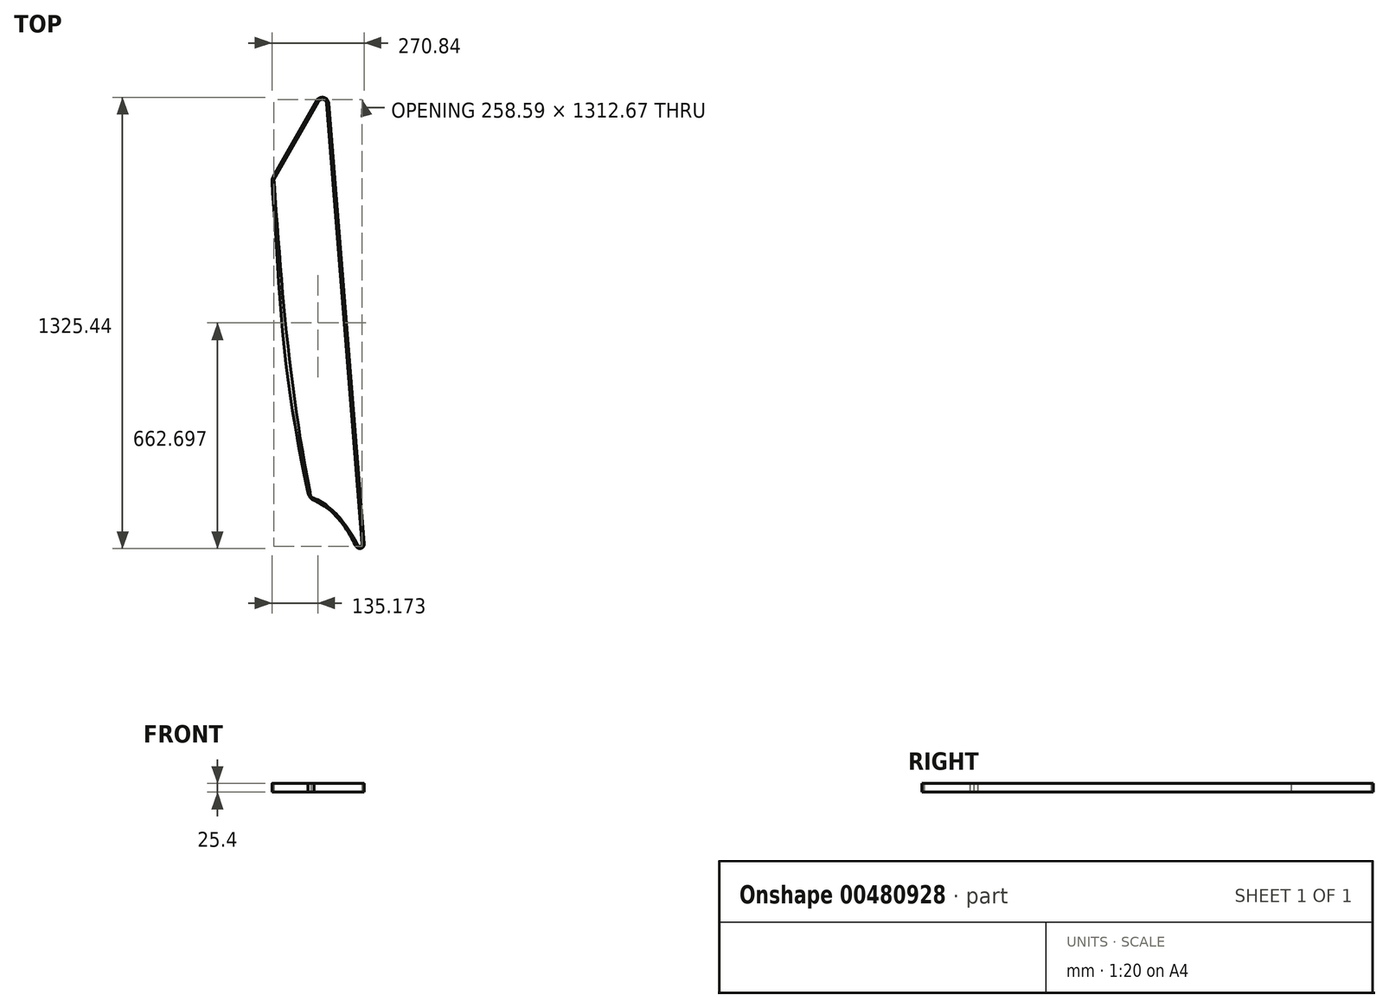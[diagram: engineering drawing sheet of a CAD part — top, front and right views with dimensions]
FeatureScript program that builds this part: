
annotation { "Feature Type Name" : "Feature", "Feature Type Description" : "" }
export const myFeature = defineFeature(function(context is Context, id is Id, definition is map)
    precondition{}
    {
        {
            var Q0;
            Q0=qCreatedBy(makeId("Top.planeOp"),FACE);
            var sketch = newSketch(context, id + "F0", { "sketchPlane" : qUnion([Q0])});
            skLineSegment(sketch, "E0", {"start": v(-2.57, 32.08) * mm, "end": v(-106.43, 1326.28) * mm});
            skFitSpline(sketch, "E1", {"points": [v(-109.71, 1367.2) * mm, v(-261.16, 1102.61) * mm], "startDerivative": vector(-151.45, -264.6) * mm, "endDerivative": vector(-151.45, -264.6) * mm});
            skFitSpline(sketch, "E2", {"points": [v(0, 0) * mm, v(-152.49, 170.33) * mm], "startDerivative": vector(-122.88, 253.62) * mm, "endDerivative": vector(-197.32, 68.63) * mm});
            skFitSpline(sketch, "E3", {"points": [v(-152.49, 170.33) * mm, v(-261.16, 1102.61) * mm], "startDerivative": vector(-188.74, 943.72) * mm, "endDerivative": vector(-68.63, 995.2) * mm});
            skArc(sketch, "E4.filletArc", {"start": v(-14.5, 28.59) * mm, "mid": v(-7.12, 25.48) * mm, "end": v(-2.57, 32.08) * mm});
            skArc(sketch, "E5.filletArc", {"start": v(-155.2, 183.97) * mm, "mid": v(-150.09, 172.99) * mm, "end": v(-140.47, 165.62) * mm});
            skArc(sketch, "E6.filletArc", {"start": v(-257.33, 1109.3) * mm, "mid": v(-260.05, 1102.36) * mm, "end": v(-260.63, 1094.93) * mm});
            skArc(sketch, "E7.filletArc", {"start": v(-106.43, 1326.28) * mm, "mid": v(-116.32, 1337.65) * mm, "end": v(-130.11, 1331.57) * mm});
            skFitSpline(sketch, "E8.0", {"points": [v(-161.43, 182.75) * mm, v(-191.66, 336.36) * mm, v(-233.25, 630.39) * mm, v(-255.78, 932.63) * mm, v(-266.96, 1094.5) * mm]});
            skArc(sketch, "E8.1", {"start": v(-262.85, 1112.45) * mm, "mid": v(-266.24, 1103.78) * mm, "end": v(-266.96, 1094.5) * mm});
            skFitSpline(sketch, "E8.2", {"points": [v(-135.62, 1334.72) * mm, v(-178.03, 1260.63) * mm, v(-220.44, 1186.54) * mm, v(-262.85, 1112.45) * mm]});
            skArc(sketch, "E8.3", {"start": v(-100.1, 1326.78) * mm, "mid": v(-114.93, 1343.85) * mm, "end": v(-135.62, 1334.72) * mm});
            skLineSegment(sketch, "E9.0", {"start": v(3.76, 32.59) * mm, "end": v(-100.1, 1326.78) * mm});
            skArc(sketch, "E9.1", {"start": v(-20.1, 25.6) * mm, "mid": v(-5.33, 19.39) * mm, "end": v(3.76, 32.59) * mm});
            skFitSpline(sketch, "E9.2", {"points": [v(-20.1, 25.6) * mm, v(-28.72, 41.73) * mm, v(-46.44, 71.94) * mm, v(-75.27, 110.1) * mm, v(-101.7, 135.16) * mm, v(-124.63, 150.78) * mm, v(-136.77, 157.06) * mm, v(-143.02, 159.8) * mm]});
            skArc(sketch, "E9.3", {"start": v(-161.43, 182.75) * mm, "mid": v(-155.04, 169.01) * mm, "end": v(-143.02, 159.8) * mm});
            skSolve(sketch);
        }
        {
            var Q0;
            Q0 = qSketchRegion(id + "F0", true);
            extrude(context, id + "F1", {"entities" : qUnion([Q0]), "depth" : 25.4 * mm});
        }
        {
            var Q0;
            Q0=qCreatedBy(makeId("Right.planeOp"),FACE);
            cPlane(context, id + "F2", {"entities" : qUnion([Q0]), "cplaneType" : CPlaneType.OFFSET, "offset" : 324.87 * mm, "oppositeDirection" : true, "width" : 152.4 * mm, "height" : 152.4 * mm});
        }
        {
            var Q0;
            Q0=qCreatedBy(id+"F2.planeOp",FACE);
            var sketch = newSketch(context, id + "F3", { "sketchPlane" : qUnion([Q0])});
            skLineSegment(sketch, "E10.bottom", {"start": v(1094.5, 25.4) * mm, "end": v(182.75, 25.4) * mm});
            skLineSegment(sketch, "E10.top", {"start": v(1094.5, 15.88) * mm, "end": v(182.75, 15.87) * mm});
            skLineSegment(sketch, "E10.left", {"start": v(1094.5, 25.4) * mm, "end": v(1094.5, 15.88) * mm});
            skLineSegment(sketch, "E10.right", {"start": v(182.75, 25.4) * mm, "end": v(182.75, 15.87) * mm});
            skLineSegment(sketch, "E11", {"start": v(1094.5, 20.64) * mm, "end": v(182.75, 20.64) * mm, "construction": true});
            skLineSegment(sketch, "E12", {"start": v(1094.5, 20.64) * mm, "end": v(1090.85, 24.28) * mm});
            skLineSegment(sketch, "E13", {"start": v(1088.6, 24.28) * mm, "end": v(1086.09, 21.76) * mm});
            skPoint(sketch, "E14.visualSharp", {"position": v(1089.73, 25.4) * mm});
            skArc(sketch, "E14.filletArc", {"start": v(1090.85, 24.28) * mm, "mid": v(1089.73, 24.74) * mm, "end": v(1088.6, 24.28) * mm});
            skLineSegment(sketch, "E15", {"start": v(1083.84, 21.76) * mm, "end": v(1081.33, 24.28) * mm});
            skLineSegment(sketch, "E16", {"start": v(1079.08, 24.28) * mm, "end": v(1075.44, 20.64) * mm});
            skPoint(sketch, "E17.visualSharp", {"position": v(1084.97, 20.64) * mm});
            skArc(sketch, "E17.filletArc", {"start": v(1083.84, 21.76) * mm, "mid": v(1084.97, 21.3) * mm, "end": v(1086.09, 21.76) * mm});
            skPoint(sketch, "E18.visualSharp", {"position": v(1080.2, 25.4) * mm});
            skArc(sketch, "E18.filletArc", {"start": v(1081.33, 24.28) * mm, "mid": v(1080.2, 24.74) * mm, "end": v(1079.08, 24.28) * mm});
            skLineSegment(sketch, "E19.1.0.0", {"start": v(1069.1, 20.64) * mm, "end": v(1065.45, 24.28) * mm});
            skArc(sketch, "E19.1.0.1", {"start": v(1065.45, 24.28) * mm, "mid": v(1064.33, 24.74) * mm, "end": v(1063.2, 24.28) * mm});
            skLineSegment(sketch, "E19.1.0.2", {"start": v(1063.2, 24.28) * mm, "end": v(1060.69, 21.76) * mm});
            skArc(sketch, "E19.1.0.3", {"start": v(1058.44, 21.76) * mm, "mid": v(1059.57, 21.3) * mm, "end": v(1060.69, 21.76) * mm});
            skLineSegment(sketch, "E19.1.0.4", {"start": v(1058.44, 21.76) * mm, "end": v(1055.93, 24.28) * mm});
            skArc(sketch, "E19.1.0.5", {"start": v(1055.93, 24.28) * mm, "mid": v(1054.8, 24.74) * mm, "end": v(1053.68, 24.28) * mm});
            skLineSegment(sketch, "E19.1.0.6", {"start": v(1053.68, 24.28) * mm, "end": v(1050.04, 20.64) * mm});
            skLineSegment(sketch, "E19.2.0.0", {"start": v(1043.7, 20.64) * mm, "end": v(1040.05, 24.28) * mm});
            skArc(sketch, "E19.2.0.1", {"start": v(1040.05, 24.28) * mm, "mid": v(1038.93, 24.74) * mm, "end": v(1037.8, 24.28) * mm});
            skLineSegment(sketch, "E19.2.0.2", {"start": v(1037.8, 24.28) * mm, "end": v(1035.29, 21.76) * mm});
            skArc(sketch, "E19.2.0.3", {"start": v(1033.04, 21.76) * mm, "mid": v(1034.17, 21.3) * mm, "end": v(1035.29, 21.76) * mm});
            skLineSegment(sketch, "E19.2.0.4", {"start": v(1033.04, 21.76) * mm, "end": v(1030.53, 24.28) * mm});
            skArc(sketch, "E19.2.0.5", {"start": v(1030.53, 24.28) * mm, "mid": v(1029.4, 24.74) * mm, "end": v(1028.28, 24.28) * mm});
            skLineSegment(sketch, "E19.2.0.6", {"start": v(1028.28, 24.28) * mm, "end": v(1024.64, 20.64) * mm});
            skLineSegment(sketch, "E19.3.0.0", {"start": v(1018.3, 20.64) * mm, "end": v(1014.65, 24.28) * mm});
            skArc(sketch, "E19.3.0.1", {"start": v(1014.65, 24.28) * mm, "mid": v(1013.53, 24.74) * mm, "end": v(1012.4, 24.28) * mm});
            skLineSegment(sketch, "E19.3.0.2", {"start": v(1012.4, 24.28) * mm, "end": v(1009.89, 21.76) * mm});
            skArc(sketch, "E19.3.0.3", {"start": v(1007.64, 21.76) * mm, "mid": v(1008.77, 21.3) * mm, "end": v(1009.89, 21.76) * mm});
            skLineSegment(sketch, "E19.3.0.4", {"start": v(1007.64, 21.76) * mm, "end": v(1005.13, 24.28) * mm});
            skArc(sketch, "E19.3.0.5", {"start": v(1005.13, 24.28) * mm, "mid": v(1004, 24.74) * mm, "end": v(1002.88, 24.28) * mm});
            skLineSegment(sketch, "E19.3.0.6", {"start": v(1002.88, 24.28) * mm, "end": v(999.24, 20.64) * mm});
            skLineSegment(sketch, "E19.4.0.0", {"start": v(992.9, 20.64) * mm, "end": v(989.25, 24.28) * mm});
            skArc(sketch, "E19.4.0.1", {"start": v(989.25, 24.28) * mm, "mid": v(988.13, 24.74) * mm, "end": v(987, 24.28) * mm});
            skLineSegment(sketch, "E19.4.0.2", {"start": v(987, 24.28) * mm, "end": v(984.49, 21.76) * mm});
            skArc(sketch, "E19.4.0.3", {"start": v(982.24, 21.76) * mm, "mid": v(983.37, 21.3) * mm, "end": v(984.49, 21.76) * mm});
            skLineSegment(sketch, "E19.4.0.4", {"start": v(982.24, 21.76) * mm, "end": v(979.73, 24.28) * mm});
            skArc(sketch, "E19.4.0.5", {"start": v(979.73, 24.28) * mm, "mid": v(978.6, 24.74) * mm, "end": v(977.48, 24.28) * mm});
            skLineSegment(sketch, "E19.4.0.6", {"start": v(977.48, 24.28) * mm, "end": v(973.84, 20.64) * mm});
            skLineSegment(sketch, "E19.5.0.0", {"start": v(967.5, 20.64) * mm, "end": v(963.85, 24.28) * mm});
            skArc(sketch, "E19.5.0.1", {"start": v(963.85, 24.28) * mm, "mid": v(962.73, 24.74) * mm, "end": v(961.6, 24.28) * mm});
            skLineSegment(sketch, "E19.5.0.2", {"start": v(961.6, 24.28) * mm, "end": v(959.09, 21.76) * mm});
            skArc(sketch, "E19.5.0.3", {"start": v(956.84, 21.76) * mm, "mid": v(957.97, 21.3) * mm, "end": v(959.09, 21.76) * mm});
            skLineSegment(sketch, "E19.5.0.4", {"start": v(956.84, 21.76) * mm, "end": v(954.33, 24.28) * mm});
            skArc(sketch, "E19.5.0.5", {"start": v(954.33, 24.28) * mm, "mid": v(953.2, 24.74) * mm, "end": v(952.08, 24.28) * mm});
            skLineSegment(sketch, "E19.5.0.6", {"start": v(952.08, 24.28) * mm, "end": v(948.44, 20.64) * mm});
            skLineSegment(sketch, "E19.6.0.0", {"start": v(942.1, 20.64) * mm, "end": v(938.45, 24.28) * mm});
            skArc(sketch, "E19.6.0.1", {"start": v(938.45, 24.28) * mm, "mid": v(937.33, 24.74) * mm, "end": v(936.2, 24.28) * mm});
            skLineSegment(sketch, "E19.6.0.2", {"start": v(936.2, 24.28) * mm, "end": v(933.69, 21.76) * mm});
            skArc(sketch, "E19.6.0.3", {"start": v(931.44, 21.76) * mm, "mid": v(932.57, 21.3) * mm, "end": v(933.69, 21.76) * mm});
            skLineSegment(sketch, "E19.6.0.4", {"start": v(931.44, 21.76) * mm, "end": v(928.93, 24.28) * mm});
            skArc(sketch, "E19.6.0.5", {"start": v(928.93, 24.28) * mm, "mid": v(927.8, 24.74) * mm, "end": v(926.68, 24.28) * mm});
            skLineSegment(sketch, "E19.6.0.6", {"start": v(926.68, 24.28) * mm, "end": v(923.04, 20.64) * mm});
            skLineSegment(sketch, "E19.7.0.0", {"start": v(916.7, 20.64) * mm, "end": v(913.05, 24.28) * mm});
            skArc(sketch, "E19.7.0.1", {"start": v(913.05, 24.28) * mm, "mid": v(911.93, 24.74) * mm, "end": v(910.8, 24.28) * mm});
            skLineSegment(sketch, "E19.7.0.2", {"start": v(910.8, 24.28) * mm, "end": v(908.29, 21.76) * mm});
            skArc(sketch, "E19.7.0.3", {"start": v(906.04, 21.76) * mm, "mid": v(907.17, 21.3) * mm, "end": v(908.29, 21.76) * mm});
            skLineSegment(sketch, "E19.7.0.4", {"start": v(906.04, 21.76) * mm, "end": v(903.53, 24.28) * mm});
            skArc(sketch, "E19.7.0.5", {"start": v(903.53, 24.28) * mm, "mid": v(902.4, 24.74) * mm, "end": v(901.28, 24.28) * mm});
            skLineSegment(sketch, "E19.7.0.6", {"start": v(901.28, 24.28) * mm, "end": v(897.64, 20.64) * mm});
            skLineSegment(sketch, "E19.8.0.0", {"start": v(891.3, 20.64) * mm, "end": v(887.65, 24.28) * mm});
            skArc(sketch, "E19.8.0.1", {"start": v(887.65, 24.28) * mm, "mid": v(886.53, 24.74) * mm, "end": v(885.4, 24.28) * mm});
            skLineSegment(sketch, "E19.8.0.2", {"start": v(885.4, 24.28) * mm, "end": v(882.89, 21.76) * mm});
            skArc(sketch, "E19.8.0.3", {"start": v(880.64, 21.76) * mm, "mid": v(881.77, 21.3) * mm, "end": v(882.89, 21.76) * mm});
            skLineSegment(sketch, "E19.8.0.4", {"start": v(880.64, 21.76) * mm, "end": v(878.13, 24.28) * mm});
            skArc(sketch, "E19.8.0.5", {"start": v(878.13, 24.28) * mm, "mid": v(877, 24.74) * mm, "end": v(875.88, 24.28) * mm});
            skLineSegment(sketch, "E19.8.0.6", {"start": v(875.88, 24.28) * mm, "end": v(872.24, 20.64) * mm});
            skLineSegment(sketch, "E19.9.0.0", {"start": v(865.9, 20.64) * mm, "end": v(862.25, 24.28) * mm});
            skArc(sketch, "E19.9.0.1", {"start": v(862.25, 24.28) * mm, "mid": v(861.13, 24.74) * mm, "end": v(860, 24.28) * mm});
            skLineSegment(sketch, "E19.9.0.2", {"start": v(860, 24.28) * mm, "end": v(857.49, 21.76) * mm});
            skArc(sketch, "E19.9.0.3", {"start": v(855.24, 21.76) * mm, "mid": v(856.37, 21.3) * mm, "end": v(857.49, 21.76) * mm});
            skLineSegment(sketch, "E19.9.0.4", {"start": v(855.24, 21.76) * mm, "end": v(852.73, 24.28) * mm});
            skArc(sketch, "E19.9.0.5", {"start": v(852.73, 24.28) * mm, "mid": v(851.6, 24.74) * mm, "end": v(850.48, 24.28) * mm});
            skLineSegment(sketch, "E19.9.0.6", {"start": v(850.48, 24.28) * mm, "end": v(846.84, 20.64) * mm});
            skLineSegment(sketch, "E19.10.0.0", {"start": v(840.5, 20.64) * mm, "end": v(836.85, 24.28) * mm});
            skArc(sketch, "E19.10.0.1", {"start": v(836.85, 24.28) * mm, "mid": v(835.73, 24.74) * mm, "end": v(834.6, 24.28) * mm});
            skLineSegment(sketch, "E19.10.0.2", {"start": v(834.6, 24.28) * mm, "end": v(832.09, 21.76) * mm});
            skArc(sketch, "E19.10.0.3", {"start": v(829.84, 21.76) * mm, "mid": v(830.97, 21.3) * mm, "end": v(832.09, 21.76) * mm});
            skLineSegment(sketch, "E19.10.0.4", {"start": v(829.84, 21.76) * mm, "end": v(827.33, 24.28) * mm});
            skArc(sketch, "E19.10.0.5", {"start": v(827.33, 24.28) * mm, "mid": v(826.2, 24.74) * mm, "end": v(825.08, 24.28) * mm});
            skLineSegment(sketch, "E19.10.0.6", {"start": v(825.08, 24.28) * mm, "end": v(821.44, 20.64) * mm});
            skLineSegment(sketch, "E19.11.0.0", {"start": v(815.1, 20.64) * mm, "end": v(811.45, 24.28) * mm});
            skArc(sketch, "E19.11.0.1", {"start": v(811.45, 24.28) * mm, "mid": v(810.33, 24.74) * mm, "end": v(809.2, 24.28) * mm});
            skLineSegment(sketch, "E19.11.0.2", {"start": v(809.2, 24.28) * mm, "end": v(806.69, 21.76) * mm});
            skArc(sketch, "E19.11.0.3", {"start": v(804.44, 21.76) * mm, "mid": v(805.57, 21.3) * mm, "end": v(806.69, 21.76) * mm});
            skLineSegment(sketch, "E19.11.0.4", {"start": v(804.44, 21.76) * mm, "end": v(801.93, 24.28) * mm});
            skArc(sketch, "E19.11.0.5", {"start": v(801.93, 24.28) * mm, "mid": v(800.8, 24.74) * mm, "end": v(799.68, 24.28) * mm});
            skLineSegment(sketch, "E19.11.0.6", {"start": v(799.68, 24.28) * mm, "end": v(796.04, 20.64) * mm});
            skLineSegment(sketch, "E19.12.0.0", {"start": v(789.7, 20.64) * mm, "end": v(786.05, 24.28) * mm});
            skArc(sketch, "E19.12.0.1", {"start": v(786.05, 24.28) * mm, "mid": v(784.93, 24.74) * mm, "end": v(783.8, 24.28) * mm});
            skLineSegment(sketch, "E19.12.0.2", {"start": v(783.8, 24.28) * mm, "end": v(781.29, 21.76) * mm});
            skArc(sketch, "E19.12.0.3", {"start": v(779.04, 21.76) * mm, "mid": v(780.17, 21.3) * mm, "end": v(781.29, 21.76) * mm});
            skLineSegment(sketch, "E19.12.0.4", {"start": v(779.04, 21.76) * mm, "end": v(776.53, 24.28) * mm});
            skArc(sketch, "E19.12.0.5", {"start": v(776.53, 24.28) * mm, "mid": v(775.4, 24.74) * mm, "end": v(774.28, 24.28) * mm});
            skLineSegment(sketch, "E19.12.0.6", {"start": v(774.28, 24.28) * mm, "end": v(770.64, 20.64) * mm});
            skLineSegment(sketch, "E19.13.0.0", {"start": v(764.3, 20.64) * mm, "end": v(760.65, 24.28) * mm});
            skArc(sketch, "E19.13.0.1", {"start": v(760.65, 24.28) * mm, "mid": v(759.53, 24.74) * mm, "end": v(758.4, 24.28) * mm});
            skLineSegment(sketch, "E19.13.0.2", {"start": v(758.4, 24.28) * mm, "end": v(755.89, 21.76) * mm});
            skArc(sketch, "E19.13.0.3", {"start": v(753.64, 21.76) * mm, "mid": v(754.77, 21.3) * mm, "end": v(755.89, 21.76) * mm});
            skLineSegment(sketch, "E19.13.0.4", {"start": v(753.64, 21.76) * mm, "end": v(751.13, 24.28) * mm});
            skArc(sketch, "E19.13.0.5", {"start": v(751.13, 24.28) * mm, "mid": v(750, 24.74) * mm, "end": v(748.88, 24.28) * mm});
            skLineSegment(sketch, "E19.13.0.6", {"start": v(748.88, 24.28) * mm, "end": v(745.24, 20.64) * mm});
            skLineSegment(sketch, "E19.14.0.0", {"start": v(738.9, 20.64) * mm, "end": v(735.25, 24.28) * mm});
            skArc(sketch, "E19.14.0.1", {"start": v(735.25, 24.28) * mm, "mid": v(734.13, 24.74) * mm, "end": v(733, 24.28) * mm});
            skLineSegment(sketch, "E19.14.0.2", {"start": v(733, 24.28) * mm, "end": v(730.49, 21.76) * mm});
            skArc(sketch, "E19.14.0.3", {"start": v(728.24, 21.76) * mm, "mid": v(729.37, 21.3) * mm, "end": v(730.49, 21.76) * mm});
            skLineSegment(sketch, "E19.14.0.4", {"start": v(728.24, 21.76) * mm, "end": v(725.73, 24.28) * mm});
            skArc(sketch, "E19.14.0.5", {"start": v(725.73, 24.28) * mm, "mid": v(724.6, 24.74) * mm, "end": v(723.48, 24.28) * mm});
            skLineSegment(sketch, "E19.14.0.6", {"start": v(723.48, 24.28) * mm, "end": v(719.84, 20.64) * mm});
            skLineSegment(sketch, "E19.15.0.0", {"start": v(713.5, 20.64) * mm, "end": v(709.85, 24.28) * mm});
            skArc(sketch, "E19.15.0.1", {"start": v(709.85, 24.28) * mm, "mid": v(708.73, 24.74) * mm, "end": v(707.6, 24.28) * mm});
            skLineSegment(sketch, "E19.15.0.2", {"start": v(707.6, 24.28) * mm, "end": v(705.09, 21.76) * mm});
            skArc(sketch, "E19.15.0.3", {"start": v(702.84, 21.76) * mm, "mid": v(703.97, 21.3) * mm, "end": v(705.09, 21.76) * mm});
            skLineSegment(sketch, "E19.15.0.4", {"start": v(702.84, 21.76) * mm, "end": v(700.33, 24.28) * mm});
            skArc(sketch, "E19.15.0.5", {"start": v(700.33, 24.28) * mm, "mid": v(699.2, 24.74) * mm, "end": v(698.08, 24.28) * mm});
            skLineSegment(sketch, "E19.15.0.6", {"start": v(698.08, 24.28) * mm, "end": v(694.44, 20.64) * mm});
            skLineSegment(sketch, "E19.16.0.0", {"start": v(688.1, 20.64) * mm, "end": v(684.45, 24.28) * mm});
            skArc(sketch, "E19.16.0.1", {"start": v(684.45, 24.28) * mm, "mid": v(683.33, 24.74) * mm, "end": v(682.2, 24.28) * mm});
            skLineSegment(sketch, "E19.16.0.2", {"start": v(682.2, 24.28) * mm, "end": v(679.69, 21.76) * mm});
            skArc(sketch, "E19.16.0.3", {"start": v(677.44, 21.76) * mm, "mid": v(678.57, 21.3) * mm, "end": v(679.69, 21.76) * mm});
            skLineSegment(sketch, "E19.16.0.4", {"start": v(677.44, 21.76) * mm, "end": v(674.93, 24.28) * mm});
            skArc(sketch, "E19.16.0.5", {"start": v(674.93, 24.28) * mm, "mid": v(673.8, 24.74) * mm, "end": v(672.68, 24.28) * mm});
            skLineSegment(sketch, "E19.16.0.6", {"start": v(672.68, 24.28) * mm, "end": v(669.04, 20.64) * mm});
            skLineSegment(sketch, "E19.17.0.0", {"start": v(662.7, 20.64) * mm, "end": v(659.05, 24.28) * mm});
            skArc(sketch, "E19.17.0.1", {"start": v(659.05, 24.28) * mm, "mid": v(657.93, 24.74) * mm, "end": v(656.8, 24.28) * mm});
            skLineSegment(sketch, "E19.17.0.2", {"start": v(656.8, 24.28) * mm, "end": v(654.29, 21.76) * mm});
            skArc(sketch, "E19.17.0.3", {"start": v(652.04, 21.76) * mm, "mid": v(653.17, 21.3) * mm, "end": v(654.29, 21.76) * mm});
            skLineSegment(sketch, "E19.17.0.4", {"start": v(652.04, 21.76) * mm, "end": v(649.53, 24.28) * mm});
            skArc(sketch, "E19.17.0.5", {"start": v(649.53, 24.28) * mm, "mid": v(648.4, 24.74) * mm, "end": v(647.28, 24.28) * mm});
            skLineSegment(sketch, "E19.17.0.6", {"start": v(647.28, 24.28) * mm, "end": v(643.64, 20.64) * mm});
            skLineSegment(sketch, "E19.18.0.0", {"start": v(637.3, 20.64) * mm, "end": v(633.65, 24.28) * mm});
            skArc(sketch, "E19.18.0.1", {"start": v(633.65, 24.28) * mm, "mid": v(632.53, 24.74) * mm, "end": v(631.4, 24.28) * mm});
            skLineSegment(sketch, "E19.18.0.2", {"start": v(631.4, 24.28) * mm, "end": v(628.89, 21.76) * mm});
            skArc(sketch, "E19.18.0.3", {"start": v(626.64, 21.76) * mm, "mid": v(627.77, 21.3) * mm, "end": v(628.89, 21.76) * mm});
            skLineSegment(sketch, "E19.18.0.4", {"start": v(626.64, 21.76) * mm, "end": v(624.13, 24.28) * mm});
            skArc(sketch, "E19.18.0.5", {"start": v(624.13, 24.28) * mm, "mid": v(623, 24.74) * mm, "end": v(621.88, 24.28) * mm});
            skLineSegment(sketch, "E19.18.0.6", {"start": v(621.88, 24.28) * mm, "end": v(618.24, 20.64) * mm});
            skLineSegment(sketch, "E19.19.0.0", {"start": v(611.9, 20.64) * mm, "end": v(608.25, 24.28) * mm});
            skArc(sketch, "E19.19.0.1", {"start": v(608.25, 24.28) * mm, "mid": v(607.13, 24.74) * mm, "end": v(606, 24.28) * mm});
            skLineSegment(sketch, "E19.19.0.2", {"start": v(606, 24.28) * mm, "end": v(603.49, 21.76) * mm});
            skArc(sketch, "E19.19.0.3", {"start": v(601.24, 21.76) * mm, "mid": v(602.37, 21.3) * mm, "end": v(603.49, 21.76) * mm});
            skLineSegment(sketch, "E19.19.0.4", {"start": v(601.24, 21.76) * mm, "end": v(598.73, 24.28) * mm});
            skArc(sketch, "E19.19.0.5", {"start": v(598.73, 24.28) * mm, "mid": v(597.6, 24.74) * mm, "end": v(596.48, 24.28) * mm});
            skLineSegment(sketch, "E19.19.0.6", {"start": v(596.48, 24.28) * mm, "end": v(592.84, 20.64) * mm});
            skLineSegment(sketch, "E19.direction1", {"start": v(1094.5, 20.64) * mm, "end": v(1069.1, 20.64) * mm, "construction": true});
            skSolve(sketch);
        }
        {
            var Q0;
            Q0=sQuery(id+"F3.wireOp",EDGE,"E19.3.0.0");
            var Q1;
            Q1=sQuery(id+"F3.wireOp",EDGE,"E19.3.0.4");
            var Q2;
            Q2=sQuery(id+"F3.wireOp",EDGE,"E19.3.0.1");
            var Q3;
            Q3=sQuery(id+"F3.wireOp",EDGE,"E19.3.0.2");
            var Q4;
            Q4=sQuery(id+"F3.wireOp",EDGE,"E19.3.0.3");
            var Q5;
            Q5=sQuery(id+"F3.wireOp",EDGE,"E19.3.0.5");
            var Q6;
            Q6=sQuery(id+"F3.wireOp",EDGE,"E19.3.0.6");
            var Q7;
            Q7=sQuery(id+"F3.wireOp",EDGE,"E19.2.0.6");
            var Q8;
            Q8=sQuery(id+"F3.wireOp",EDGE,"E19.2.0.5");
            var Q9;
            Q9=sQuery(id+"F3.wireOp",EDGE,"E19.2.0.4");
            var Q10;
            Q10=sQuery(id+"F3.wireOp",EDGE,"E19.2.0.3");
            var Q11;
            Q11=sQuery(id+"F3.wireOp",EDGE,"E19.2.0.2");
            var Q12;
            Q12=sQuery(id+"F3.wireOp",EDGE,"E19.2.0.1");
            var Q13;
            Q13=sQuery(id+"F3.wireOp",EDGE,"E19.2.0.0");
            var Q14;
            Q14=sQuery(id+"F3.wireOp",EDGE,"E19.1.0.6");
            var Q15;
            Q15=sQuery(id+"F3.wireOp",EDGE,"E19.1.0.5");
            var Q16;
            Q16=sQuery(id+"F3.wireOp",EDGE,"E19.1.0.4");
            var Q17;
            Q17=sQuery(id+"F3.wireOp",EDGE,"E19.1.0.3");
            var Q18;
            Q18=sQuery(id+"F3.wireOp",EDGE,"E19.1.0.2");
            var Q19;
            Q19=sQuery(id+"F3.wireOp",EDGE,"E19.1.0.1");
            var Q20;
            Q20=sQuery(id+"F3.wireOp",EDGE,"E19.1.0.0");
            extrude(context, id + "F4", {"bodyType" : ToolBodyType.SURFACE, "surfaceEntities" : qUnion([Q0, Q1, Q2, Q3, Q4, Q5, Q6, Q7, Q8, Q9, Q10, Q11, Q12, Q13, Q14, Q15, Q16, Q17, Q18, Q19, Q20]), "endBound" : BoundingType.THROUGH_ALL, "depth" : 25.4 * mm});
        }
    });
